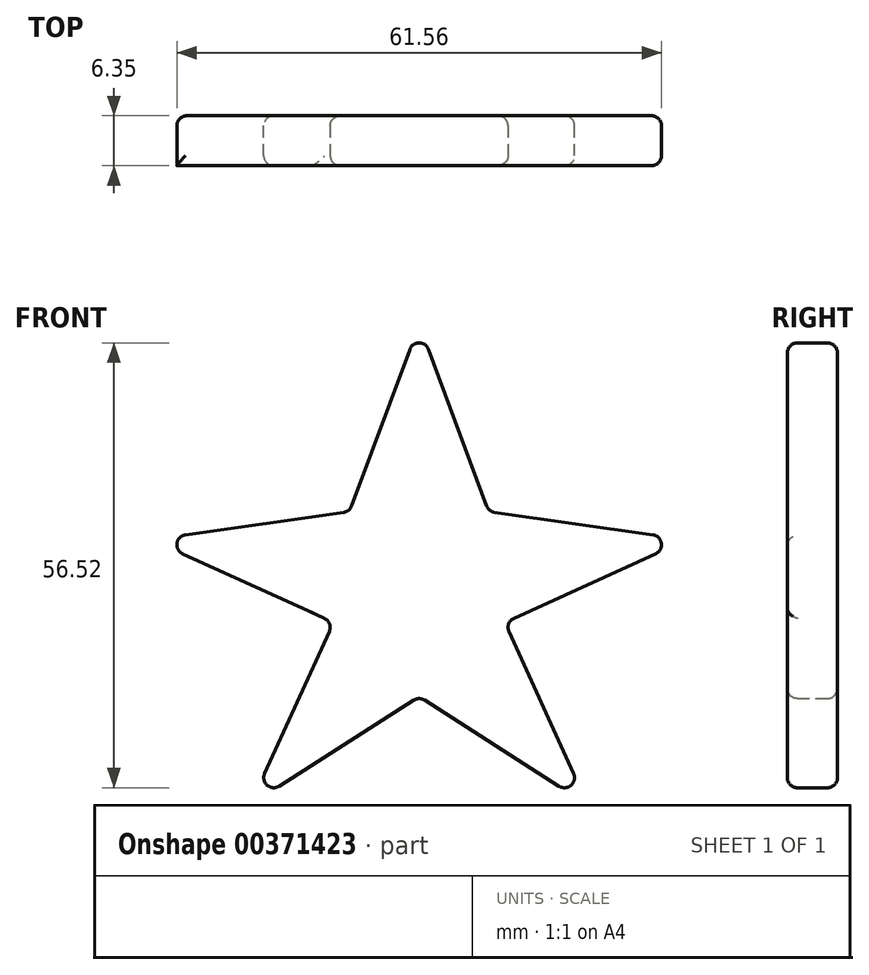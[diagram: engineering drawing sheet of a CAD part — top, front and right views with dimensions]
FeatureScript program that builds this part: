
annotation { "Feature Type Name" : "Feature", "Feature Type Description" : "" }
export const myFeature = defineFeature(function(context is Context, id is Id, definition is map)
    precondition{}
    {
        {
            var Q0;
            Q0=qCreatedBy(makeId("Front.planeOp"),FACE);
            var sketch = newSketch(context, id + "F0", { "sketchPlane" : qUnion([Q0])});
            skLineSegment(sketch, "E0", {"start": v(-8.85, 5.1) * mm, "end": v(-34, 1.55) * mm});
            skLineSegment(sketch, "E1", {"start": v(-34, 1.55) * mm, "end": v(-10.88, -8.97) * mm});
            skLineSegment(sketch, "E2", {"start": v(-10.88, -8.97) * mm, "end": v(-21.4, -32.09) * mm});
            skLineSegment(sketch, "E3", {"start": v(-21.4, -32.09) * mm, "end": v(0, -18.41) * mm});
            skPoint(sketch, "E4.start.orphan", {"position": v(0, 38.15) * mm});
            skLineSegment(sketch, "E5", {"start": v(-8.85, 5.1) * mm, "end": v(0, 28.91) * mm});
            skLineSegment(sketch, "E6", {"start": v(0, 38.15) * mm, "end": v(0, -38.05) * mm});
            skLineSegment(sketch, "E7.MirrorCS", {"start": v(8.85, 5.1) * mm, "end": v(0, 28.91) * mm});
            skLineSegment(sketch, "E8.MirrorCS", {"start": v(8.85, 5.1) * mm, "end": v(34, 1.55) * mm});
            skLineSegment(sketch, "E9.MirrorCS", {"start": v(34, 1.55) * mm, "end": v(10.88, -8.97) * mm});
            skLineSegment(sketch, "E10.MirrorCS", {"start": v(10.88, -8.97) * mm, "end": v(21.4, -32.09) * mm});
            skLineSegment(sketch, "E11.MirrorCS", {"start": v(21.4, -32.09) * mm, "end": v(0, -18.41) * mm});
            skSolve(sketch);
        }
        {
            var Q0;
            Q0 = qSketchRegion(id + "F0", true);
            extrude(context, id + "F1", {"entities" : qUnion([Q0]), "depth" : 6.35 * mm});
        }
        {
            var Q0;
            Q0=makeQuery(id+"F1.opExtrude","CAP_EDGE",EDGE,{"disambiguationData":[OSD([sQuery(id+"F0.wireOp",EDGE,"E3")])],"isStart":true});
            var Q1;
            Q1=makeQuery(id+"F1.opExtrude","CAP_EDGE",EDGE,{"disambiguationData":[OSD([sQuery(id+"F0.wireOp",EDGE,"E3")])],"isStart":false});
            var Q2;
            Q2=makeQuery(id+"F1.opExtrude","CAP_EDGE",EDGE,{"disambiguationData":[OSD([sQuery(id+"F0.wireOp",EDGE,"E11.MirrorCS")])],"isStart":true});
            var Q3;
            Q3=makeQuery(id+"F1.opExtrude","CAP_EDGE",EDGE,{"disambiguationData":[OSD([sQuery(id+"F0.wireOp",EDGE,"E11.MirrorCS")])],"isStart":false});
            var Q4;
            Q4=makeQuery(id+"F1.opExtrude","CAP_EDGE",EDGE,{"disambiguationData":[OSD([sQuery(id+"F0.wireOp",EDGE,"E10.MirrorCS")])],"isStart":true});
            var Q5;
            Q5=makeQuery(id+"F1.opExtrude","CAP_EDGE",EDGE,{"disambiguationData":[OSD([sQuery(id+"F0.wireOp",EDGE,"E10.MirrorCS")])],"isStart":false});
            var Q6;
            Q6=makeQuery(id+"F1.opExtrude","CAP_EDGE",EDGE,{"disambiguationData":[OSD([sQuery(id+"F0.wireOp",EDGE,"E9.MirrorCS")])],"isStart":false});
            var Q7;
            Q7=makeQuery(id+"F1.opExtrude","CAP_EDGE",EDGE,{"disambiguationData":[OSD([sQuery(id+"F0.wireOp",EDGE,"E9.MirrorCS")])],"isStart":true});
            var Q8;
            Q8=makeQuery(id+"F1.opExtrude","CAP_EDGE",EDGE,{"disambiguationData":[OSD([sQuery(id+"F0.wireOp",EDGE,"E8.MirrorCS")])],"isStart":false});
            var Q9;
            Q9=makeQuery(id+"F1.opExtrude","CAP_EDGE",EDGE,{"disambiguationData":[OSD([sQuery(id+"F0.wireOp",EDGE,"E8.MirrorCS")])],"isStart":true});
            var Q10;
            Q10=makeQuery(id+"F1.opExtrude","SWEPT_FACE",FACE,{"disambiguationData":[OSD([sQuery(id+"F0.wireOp",EDGE,"E5")])]});
            var Q11;
            Q11=makeQuery(id+"F1.opExtrude","SWEPT_FACE",FACE,{"disambiguationData":[OSD([sQuery(id+"F0.wireOp",EDGE,"E7.MirrorCS")])]});
            var Q12;
            Q12=makeQuery(id+"F1.opExtrude","SWEPT_FACE",FACE,{"disambiguationData":[OSD([sQuery(id+"F0.wireOp",EDGE,"E9.MirrorCS")])]});
            var Q13;
            Q13=makeQuery(id+"F1.opExtrude","SWEPT_FACE",FACE,{"disambiguationData":[OSD([sQuery(id+"F0.wireOp",EDGE,"E10.MirrorCS")])]});
            var Q14;
            Q14=makeQuery(id+"F1.opExtrude","SWEPT_FACE",FACE,{"disambiguationData":[OSD([sQuery(id+"F0.wireOp",EDGE,"E11.MirrorCS")])]});
            var Q15;
            Q15=makeQuery(id+"F1.opExtrude","SWEPT_FACE",FACE,{"disambiguationData":[OSD([sQuery(id+"F0.wireOp",EDGE,"E2")])]});
            var Q16;
            Q16=makeQuery(id+"F1.opExtrude","SWEPT_FACE",FACE,{"disambiguationData":[OSD([sQuery(id+"F0.wireOp",EDGE,"E0")])]});
            var Q17;
            Q17=makeQuery(id+"F1.opExtrude","CAP_FACE",FACE,{"disambiguationData":[OSD([sQuery(id+"F0.wireOp",EDGE,"E0"),sQuery(id+"F0.wireOp",EDGE,"E1"),sQuery(id+"F0.wireOp",EDGE,"E2"),sQuery(id+"F0.wireOp",EDGE,"E3"),sQuery(id+"F0.wireOp",EDGE,"E5"),sQuery(id+"F0.wireOp",EDGE,"E7.MirrorCS"),sQuery(id+"F0.wireOp",EDGE,"E8.MirrorCS"),sQuery(id+"F0.wireOp",EDGE,"E9.MirrorCS"),sQuery(id+"F0.wireOp",EDGE,"E10.MirrorCS"),sQuery(id+"F0.wireOp",EDGE,"E11.MirrorCS")])],"isStart":true});
            fillet(context, id + "F2", {"entities" : qUnion([Q0, Q1, Q2, Q3, Q4, Q5, Q6, Q7, Q8, Q9, Q10, Q11, Q12, Q13, Q14, Q15, Q16, Q17]), "radius" : 1.27 * mm, "tangentPropagation" : true, "allowEdgeOverflow" : false});
        }
    });
